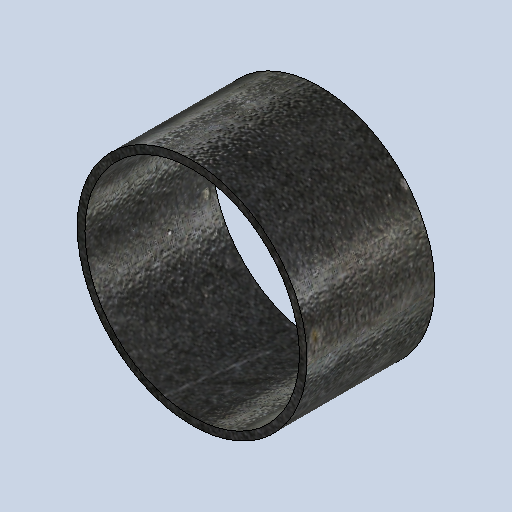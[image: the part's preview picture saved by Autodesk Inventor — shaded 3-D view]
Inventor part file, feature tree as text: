
AUTODESK INVENTOR PART (.ipt)
format: ipt  version: 2025 (Build 290162010, 162A)  size: 286,208 bytes
history: native  units: mm
features: extrude x1, sketch x1
ambient origin geometry x8: Origin, YZ Plane, XZ Plane, XY Plane, X Axis, Y Axis, Z Axis, Center Point
bodies: Solid1 (feature_tree)
feature tree (2):
  extrude  "Extrusion1"  Depth=50.0mm
  sketch  "Sketch1"  dims[d0=90.0mm d1=3.0mm d2=50.0mm d3=0.0mm]
